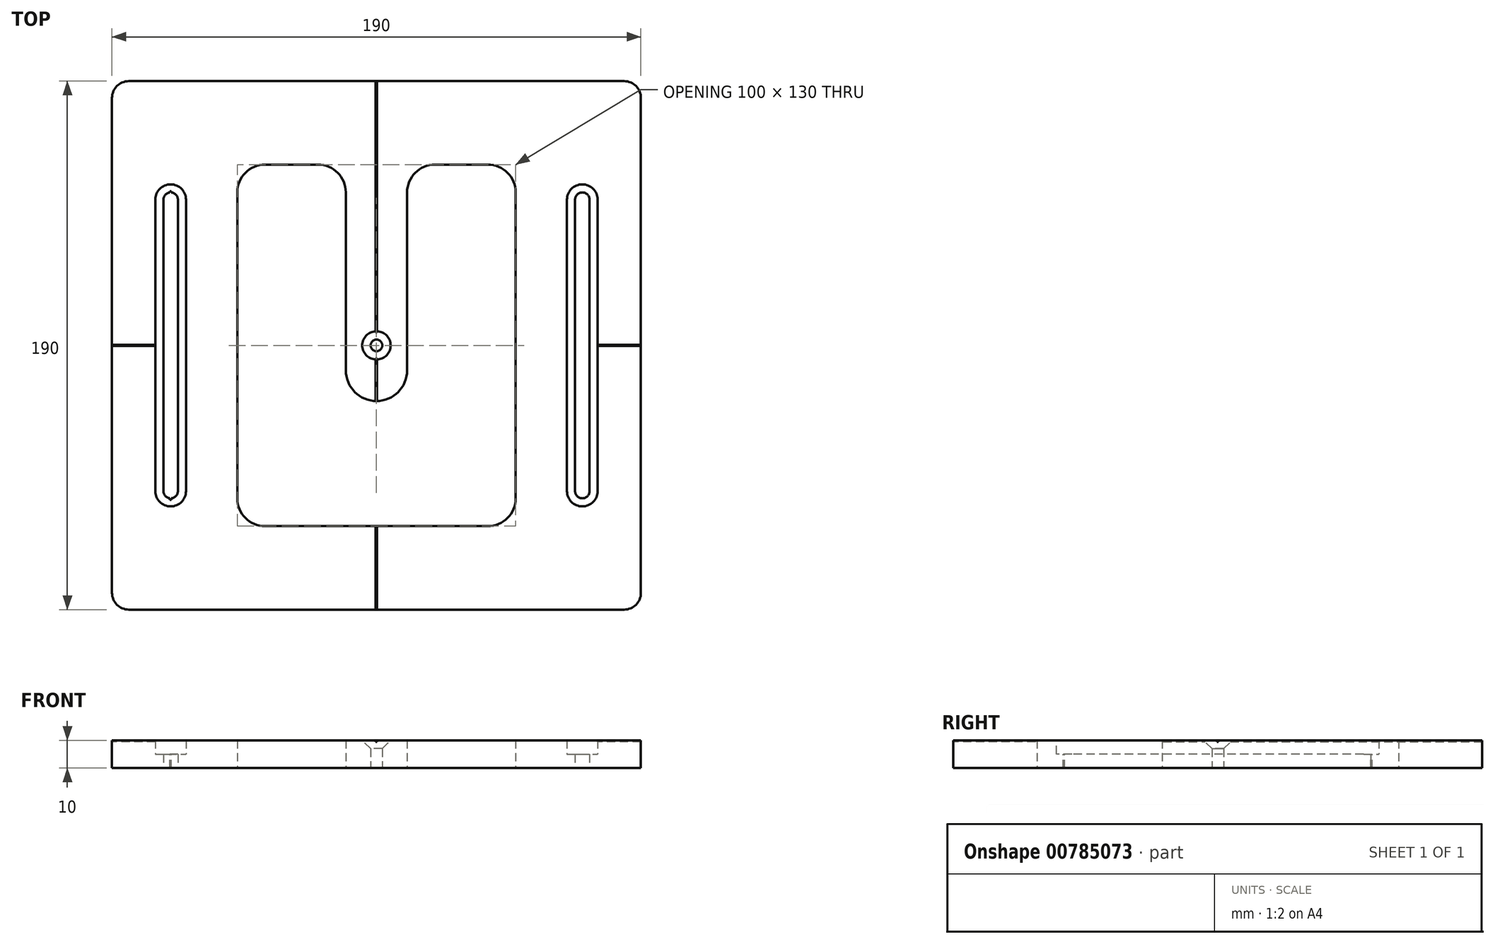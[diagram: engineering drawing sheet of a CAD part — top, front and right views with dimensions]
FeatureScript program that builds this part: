
annotation { "Feature Type Name" : "Feature", "Feature Type Description" : "" }
export const myFeature = defineFeature(function(context is Context, id is Id, definition is map)
    precondition{}
    {
        {
            var Q0;
            Q0=qCreatedBy(makeId("Top.planeOp"),FACE);
            var sketch = newSketch(context, id + "F0", { "sketchPlane" : qUnion([Q0])});
            skLineSegment(sketch, "E0.bottom", {"start": v(95, 95) * mm, "end": v(-95, 95) * mm});
            skLineSegment(sketch, "E0.top", {"start": v(95, -95) * mm, "end": v(-95, -95) * mm});
            skLineSegment(sketch, "E0.left", {"start": v(95, 95) * mm, "end": v(95, -95) * mm});
            skLineSegment(sketch, "E0.right", {"start": v(-95, 95) * mm, "end": v(-95, -95) * mm});
            skPoint(sketch, "E0.middle", {"position": v(0, 0) * mm});
            skLineSegment(sketch, "E1.bottom", {"start": v(40, -65) * mm, "end": v(-40, -65) * mm});
            skLineSegment(sketch, "E1.top", {"start": v(40, 65) * mm, "end": v(21, 65) * mm});
            skLineSegment(sketch, "E1.left", {"start": v(50, -55) * mm, "end": v(50, 55) * mm});
            skLineSegment(sketch, "E1.right", {"start": v(-50, -55) * mm, "end": v(-50, 55) * mm});
            skLineSegment(sketch, "E2", {"start": v(-95, 0) * mm, "end": v(-50, 0) * mm, "construction": true});
            skLineSegment(sketch, "E3.bottom", {"start": v(-76.54, 55) * mm, "end": v(-71.34, 55) * mm});
            skLineSegment(sketch, "E3.top", {"start": v(-76.54, -55) * mm, "end": v(-71.34, -55) * mm});
            skLineSegment(sketch, "E3.left", {"start": v(-76.54, 55) * mm, "end": v(-76.54, -55) * mm});
            skLineSegment(sketch, "E3.right", {"start": v(-71.34, 55) * mm, "end": v(-71.34, -55) * mm});
            skLineSegment(sketch, "E4.MirrorCS", {"start": v(-71.34, -55) * mm, "end": v(-71.34, 55) * mm});
            skLineSegment(sketch, "E5.MirrorCS", {"start": v(-76.54, -55) * mm, "end": v(-76.54, 55) * mm});
            skLineSegment(sketch, "E6.bottom", {"start": v(0, -20) * mm, "end": v(0, -20) * mm});
            skLineSegment(sketch, "E6.left", {"start": v(11, -9) * mm, "end": v(11, 55) * mm});
            skLineSegment(sketch, "E6.right", {"start": v(-11, -9) * mm, "end": v(-11, 55) * mm});
            skPoint(sketch, "E6.middle", {"position": v(0, 22.5) * mm});
            skPoint(sketch, "E7.visualSharp", {"position": v(-11, -20) * mm});
            skArc(sketch, "E7.filletArc", {"start": v(-11, -9) * mm, "mid": v(-7.78, -16.78) * mm, "end": v(0, -20) * mm});
            skPoint(sketch, "E8.visualSharp", {"position": v(11, -20) * mm});
            skArc(sketch, "E8.filletArc", {"start": v(0, -20) * mm, "mid": v(7.78, -16.78) * mm, "end": v(11, -9) * mm});
            skPoint(sketch, "E9.visualSharp", {"position": v(-50, 65) * mm});
            skArc(sketch, "E9.filletArc", {"start": v(-40, 65) * mm, "mid": v(-47.07, 62.07) * mm, "end": v(-50, 55) * mm});
            skPoint(sketch, "E10.visualSharp", {"position": v(50, 65) * mm});
            skArc(sketch, "E10.filletArc", {"start": v(50, 55) * mm, "mid": v(47.07, 62.07) * mm, "end": v(40, 65) * mm});
            skPoint(sketch, "E11.visualSharp", {"position": v(50, -65) * mm});
            skArc(sketch, "E11.filletArc", {"start": v(40, -65) * mm, "mid": v(47.07, -62.07) * mm, "end": v(50, -55) * mm});
            skPoint(sketch, "E12.visualSharp", {"position": v(-50, -65) * mm});
            skArc(sketch, "E12.filletArc", {"start": v(-50, -55) * mm, "mid": v(-47.07, -62.07) * mm, "end": v(-40, -65) * mm});
            skLineSegment(sketch, "E13", {"start": v(-21, 65) * mm, "end": v(-40, 65) * mm});
            skCircle(sketch, "E14", {"center": v(0, 0) * mm, "radius": 2.1 * mm});
            skLineSegment(sketch, "E15.0", {"start": v(-79.44, 57.9) * mm, "end": v(-68.44, 57.9) * mm});
            skLineSegment(sketch, "E15.1", {"start": v(-79.44, 57.9) * mm, "end": v(-79.44, -57.9) * mm});
            skLineSegment(sketch, "E15.2", {"start": v(-79.44, -57.9) * mm, "end": v(-68.44, -57.9) * mm});
            skLineSegment(sketch, "E15.3", {"start": v(-68.44, -57.9) * mm, "end": v(-68.44, 57.9) * mm});
            skPoint(sketch, "E16.visualSharp", {"position": v(11, 65) * mm});
            skArc(sketch, "E16.filletArc", {"start": v(21, 65) * mm, "mid": v(13.93, 62.07) * mm, "end": v(11, 55) * mm});
            skPoint(sketch, "E17.visualSharp", {"position": v(-11, 65) * mm});
            skArc(sketch, "E17.filletArc", {"start": v(-11, 55) * mm, "mid": v(-13.93, 62.07) * mm, "end": v(-21, 65) * mm});
            skLineSegment(sketch, "E18.MirrorCS", {"start": v(68.44, -57.9) * mm, "end": v(68.44, 57.9) * mm});
            skLineSegment(sketch, "E19.MirrorCS", {"start": v(79.44, 57.9) * mm, "end": v(68.44, 57.9) * mm});
            skLineSegment(sketch, "E20.MirrorCS", {"start": v(79.44, 57.9) * mm, "end": v(79.44, -57.9) * mm});
            skLineSegment(sketch, "E21.MirrorCS", {"start": v(79.44, -57.9) * mm, "end": v(68.44, -57.9) * mm});
            skLineSegment(sketch, "E22.MirrorCS", {"start": v(71.34, -55) * mm, "end": v(71.34, 55) * mm});
            skLineSegment(sketch, "E23.MirrorCS", {"start": v(76.54, -55) * mm, "end": v(71.34, -55) * mm});
            skLineSegment(sketch, "E24.MirrorCS", {"start": v(76.54, 55) * mm, "end": v(76.54, -55) * mm});
            skLineSegment(sketch, "E25.MirrorCS", {"start": v(76.54, 55) * mm, "end": v(71.34, 55) * mm});
            skLineSegment(sketch, "E26.bottom", {"start": v(0.25, -65.5) * mm, "end": v(-0.25, -65.5) * mm});
            skLineSegment(sketch, "E26.top", {"start": v(0.25, -64.5) * mm, "end": v(-0.25, -64.5) * mm});
            skLineSegment(sketch, "E26.left", {"start": v(0.25, -65.5) * mm, "end": v(0.25, -64.5) * mm});
            skLineSegment(sketch, "E26.right", {"start": v(-0.25, -65.5) * mm, "end": v(-0.25, -64.5) * mm});
            skPoint(sketch, "E26.middle", {"position": v(0, -65) * mm});
            skLineSegment(sketch, "E27.bottom", {"start": v(0.25, -19.5) * mm, "end": v(-0.25, -19.5) * mm});
            skLineSegment(sketch, "E27.top", {"start": v(0.25, -20.5) * mm, "end": v(-0.25, -20.5) * mm});
            skLineSegment(sketch, "E27.left", {"start": v(0.25, -19.5) * mm, "end": v(0.25, -20.5) * mm});
            skLineSegment(sketch, "E27.right", {"start": v(-0.25, -19.5) * mm, "end": v(-0.25, -20.5) * mm});
            skPoint(sketch, "E27.middle", {"position": v(0, -20) * mm});
            skSolve(sketch);
        }
        {
            var Q0;
            Q0=makeQuery(id+"F0.imprint","IMPRINT",FACE,{"disambiguationData":[TD([[makeQuery(id+"F0.imprint","IMPRINT",EDGE,{"derivedFrom":sQuery(id+"F0.wireOp",EDGE,"E0.bottom")}),1.0]])]});
            var Q1;
            {var subQ1=sQuery(id+"F0.wireOp",EDGE,"E27.bottom");Q1=makeQuery(id+"F0.imprint","IMPRINT",FACE,{"disambiguationData":[TD([[makeQuery(id+"F0.imprint","IMPRINT",EDGE,{"derivedFrom":subQ1}),1.0]])]});}
            var Q2;
            {var subQ5=sQuery(id+"F0.wireOp",EDGE,"E26.bottom");Q2=makeQuery(id+"F0.imprint","IMPRINT",FACE,{"disambiguationData":[TD([[makeQuery(id+"F0.imprint","IMPRINT",EDGE,{"derivedFrom":subQ5}),-1.0]])]});}
            extrude(context, id + "F1", {"entities" : qUnion([Q0, Q1, Q2]), "depth" : 10 * mm, "offsetDistance" : 25 * mm});
        }
        {
            var Q0;
            Q0=makeQuery(id+"F0.imprint","IMPRINT",FACE,{"disambiguationData":[TD([[makeQuery(id+"F0.imprint","IMPRINT",EDGE,{"derivedFrom":sQuery(id+"F0.wireOp",EDGE,"E3.bottom")}),1.0]])]});
            var Q1;
            Q1=makeQuery(id+"F0.imprint","IMPRINT",FACE,{"disambiguationData":[TD([[makeQuery(id+"F0.imprint","IMPRINT",EDGE,{"derivedFrom":sQuery(id+"F0.wireOp",EDGE,"E18.MirrorCS")}),-1.0]])]});
            extrude(context, id + "F2", {"entities" : qUnion([Q0, Q1]), "operationType" : NewBodyOperationType.ADD, "depth" : 5 * mm, "offsetDistance" : 25 * mm});
        }
        {
            var Q0;
            Q0=makeQuery(id+"F2.opExtrude","SWEPT_EDGE",EDGE,{"disambiguationData":[OSD([sQuery(id+"F0.wireOp",EDGE,"E3.bottom"),sQuery(id+"F0.wireOp",EDGE,"E3.left")])]});
            var Q1;
            Q1=makeQuery(id+"F2.opExtrude","SWEPT_EDGE",EDGE,{"disambiguationData":[OSD([sQuery(id+"F0.wireOp",EDGE,"E3.bottom"),sQuery(id+"F0.wireOp",EDGE,"E3.right")])]});
            var Q2;
            Q2=makeQuery(id+"F2.opExtrude","SWEPT_EDGE",EDGE,{"disambiguationData":[OSD([sQuery(id+"F0.wireOp",EDGE,"E3.top"),sQuery(id+"F0.wireOp",EDGE,"E3.left")])]});
            var Q3;
            Q3=makeQuery(id+"F2.opExtrude","SWEPT_EDGE",EDGE,{"disambiguationData":[OSD([sQuery(id+"F0.wireOp",EDGE,"E3.top"),sQuery(id+"F0.wireOp",EDGE,"E3.right")])]});
            var Q4;
            Q4=makeQuery(id+"F2.opExtrude","SWEPT_EDGE",EDGE,{"disambiguationData":[OSD([sQuery(id+"F0.wireOp",EDGE,"E23.MirrorCS"),sQuery(id+"F0.wireOp",EDGE,"E24.MirrorCS")])]});
            var Q5;
            Q5=makeQuery(id+"F2.opExtrude","SWEPT_EDGE",EDGE,{"disambiguationData":[OSD([sQuery(id+"F0.wireOp",EDGE,"E22.MirrorCS"),sQuery(id+"F0.wireOp",EDGE,"E23.MirrorCS")])]});
            var Q6;
            Q6=makeQuery(id+"F2.opExtrude","SWEPT_EDGE",EDGE,{"disambiguationData":[OSD([sQuery(id+"F0.wireOp",EDGE,"E22.MirrorCS"),sQuery(id+"F0.wireOp",EDGE,"E25.MirrorCS")])]});
            var Q7;
            Q7=makeQuery(id+"F2.opExtrude","SWEPT_EDGE",EDGE,{"disambiguationData":[OSD([sQuery(id+"F0.wireOp",EDGE,"E24.MirrorCS"),sQuery(id+"F0.wireOp",EDGE,"E25.MirrorCS")])]});
            fillet(context, id + "F3", {"entities" : qUnion([Q0, Q1, Q2, Q3, Q4, Q5, Q6, Q7]), "radius" : 2.6 * mm, "tangentPropagation" : true, "allowEdgeOverflow" : false});
        }
        {
            var Q0;
            Q0=makeQuery(id+"F1.opExtrude","SWEPT_EDGE",EDGE,{"disambiguationData":[OSD([sQuery(id+"F0.wireOp",EDGE,"E15.0"),sQuery(id+"F0.wireOp",EDGE,"E15.1")])]});
            var Q1;
            Q1=makeQuery(id+"F1.opExtrude","SWEPT_EDGE",EDGE,{"disambiguationData":[OSD([sQuery(id+"F0.wireOp",EDGE,"E15.0"),sQuery(id+"F0.wireOp",EDGE,"E15.3")])]});
            var Q2;
            Q2=makeQuery(id+"F1.opExtrude","SWEPT_EDGE",EDGE,{"disambiguationData":[OSD([sQuery(id+"F0.wireOp",EDGE,"E19.MirrorCS"),sQuery(id+"F0.wireOp",EDGE,"E20.MirrorCS")])]});
            var Q3;
            Q3=makeQuery(id+"F1.opExtrude","SWEPT_EDGE",EDGE,{"disambiguationData":[OSD([sQuery(id+"F0.wireOp",EDGE,"E18.MirrorCS"),sQuery(id+"F0.wireOp",EDGE,"E19.MirrorCS")])]});
            var Q4;
            Q4=makeQuery(id+"F1.opExtrude","SWEPT_EDGE",EDGE,{"disambiguationData":[OSD([sQuery(id+"F0.wireOp",EDGE,"E18.MirrorCS"),sQuery(id+"F0.wireOp",EDGE,"E21.MirrorCS")])]});
            var Q5;
            Q5=makeQuery(id+"F1.opExtrude","SWEPT_EDGE",EDGE,{"disambiguationData":[OSD([sQuery(id+"F0.wireOp",EDGE,"E20.MirrorCS"),sQuery(id+"F0.wireOp",EDGE,"E21.MirrorCS")])]});
            var Q6;
            Q6=makeQuery(id+"F1.opExtrude","SWEPT_EDGE",EDGE,{"disambiguationData":[OSD([sQuery(id+"F0.wireOp",EDGE,"E15.1"),sQuery(id+"F0.wireOp",EDGE,"E15.2")])]});
            var Q7;
            Q7=makeQuery(id+"F1.opExtrude","SWEPT_EDGE",EDGE,{"disambiguationData":[OSD([sQuery(id+"F0.wireOp",EDGE,"E15.2"),sQuery(id+"F0.wireOp",EDGE,"E15.3")])]});
            fillet(context, id + "F4", {"entities" : qUnion([Q0, Q1, Q2, Q3, Q4, Q5, Q6, Q7]), "radius" : 5.5 * mm, "tangentPropagation" : true, "allowEdgeOverflow" : false});
        }
        {
            var Q0;
            Q0=makeQuery(id+"F2.opExtrude","CAP_FACE",FACE,{"disambiguationData":[OSD([sQuery(id+"F0.wireOp",EDGE,"E3.bottom"),sQuery(id+"F0.wireOp",EDGE,"E3.top"),sQuery(id+"F0.wireOp",EDGE,"E3.right"),sQuery(id+"F0.wireOp",EDGE,"E3.left"),sQuery(id+"F0.wireOp",EDGE,"E15.0"),sQuery(id+"F0.wireOp",EDGE,"E15.1"),sQuery(id+"F0.wireOp",EDGE,"E15.2"),sQuery(id+"F0.wireOp",EDGE,"E15.3")])],"isStart":false});
            var sketch = newSketch(context, id + "F5", { "sketchPlane" : qUnion([Q0])});
            skLineSegment(sketch, "E28.bottom", {"start": v(-73.69, 54.5) * mm, "end": v(-74.19, 54.5) * mm});
            skLineSegment(sketch, "E28.top", {"start": v(-73.69, 55.5) * mm, "end": v(-74.19, 55.5) * mm});
            skLineSegment(sketch, "E28.left", {"start": v(-73.69, 54.5) * mm, "end": v(-73.69, 55.5) * mm});
            skLineSegment(sketch, "E28.right", {"start": v(-74.19, 54.5) * mm, "end": v(-74.19, 55.5) * mm});
            skPoint(sketch, "E28.middle", {"position": v(-73.94, 55) * mm});
            skLineSegment(sketch, "E29.bottom", {"start": v(-73.69, -55.5) * mm, "end": v(-74.19, -55.5) * mm});
            skLineSegment(sketch, "E29.top", {"start": v(-73.69, -54.5) * mm, "end": v(-74.19, -54.5) * mm});
            skLineSegment(sketch, "E29.left", {"start": v(-73.69, -55.5) * mm, "end": v(-73.69, -54.5) * mm});
            skLineSegment(sketch, "E29.right", {"start": v(-74.19, -55.5) * mm, "end": v(-74.19, -54.5) * mm});
            skPoint(sketch, "E29.middle", {"position": v(-73.94, -55) * mm});
            skSolve(sketch);
        }
        {
            var Q0;
            {var subQ0=sQuery(id+"F5.wireOp",EDGE,"E29.bottom");Q0=makeQuery(id+"F5.imprint","IMPRINT",FACE,{"disambiguationData":[TD([[makeQuery(id+"F5.imprint","IMPRINT",EDGE,{"derivedFrom":subQ0}),-1.0]])]});}
            var Q1;
            {var subQ0=sQuery(id+"F5.wireOp",EDGE,"E28.top");Q1=makeQuery(id+"F5.imprint","IMPRINT",FACE,{"disambiguationData":[TD([[makeQuery(id+"F5.imprint","IMPRINT",EDGE,{"derivedFrom":subQ0}),1.0]])]});}
            extrude(context, id + "F6", {"entities" : qUnion([Q0, Q1]), "operationType" : NewBodyOperationType.REMOVE, "oppositeDirection" : true, "depth" : 25 * mm, "offsetDistance" : 25 * mm});
        }
        {
            var Q0;
            Q0=makeQuery(id+"F1.opExtrude","CAP_FACE",FACE,{"disambiguationData":[OSD([sQuery(id+"F0.wireOp",EDGE,"E0.bottom"),sQuery(id+"F0.wireOp",EDGE,"E0.top"),sQuery(id+"F0.wireOp",EDGE,"E0.left"),sQuery(id+"F0.wireOp",EDGE,"E0.right"),sQuery(id+"F0.wireOp",EDGE,"E1.bottom"),sQuery(id+"F0.wireOp",EDGE,"E1.top"),sQuery(id+"F0.wireOp",EDGE,"E1.left"),sQuery(id+"F0.wireOp",EDGE,"E1.right"),sQuery(id+"F0.wireOp",EDGE,"E6.left"),sQuery(id+"F0.wireOp",EDGE,"E6.right"),sQuery(id+"F0.wireOp",EDGE,"E7.filletArc"),sQuery(id+"F0.wireOp",EDGE,"E8.filletArc"),sQuery(id+"F0.wireOp",EDGE,"E9.filletArc"),sQuery(id+"F0.wireOp",EDGE,"E10.filletArc"),sQuery(id+"F0.wireOp",EDGE,"E11.filletArc"),sQuery(id+"F0.wireOp",EDGE,"E12.filletArc"),sQuery(id+"F0.wireOp",EDGE,"E13"),sQuery(id+"F0.wireOp",EDGE,"0993da1e-e7eb-4dab-95c8-7e407798bd87.0"),sQuery(id+"F0.wireOp",EDGE,"E15.0"),sQuery(id+"F0.wireOp",EDGE,"E15.1"),sQuery(id+"F0.wireOp",EDGE,"E15.2"),sQuery(id+"F0.wireOp",EDGE,"E15.3"),sQuery(id+"F0.wireOp",EDGE,"E16.filletArc"),sQuery(id+"F0.wireOp",EDGE,"E17.filletArc"),sQuery(id+"F0.wireOp",EDGE,"E18.MirrorCS"),sQuery(id+"F0.wireOp",EDGE,"E19.MirrorCS"),sQuery(id+"F0.wireOp",EDGE,"E20.MirrorCS"),sQuery(id+"F0.wireOp",EDGE,"E21.MirrorCS")])],"isStart":false});
            var sketch = newSketch(context, id + "F7", { "sketchPlane" : qUnion([Q0])});
            skLineSegment(sketch, "E30.bottom", {"start": v(-0.25, -19.6) * mm, "end": v(0.25, -19.6) * mm});
            skLineSegment(sketch, "E30.top", {"start": v(-0.25, -20.4) * mm, "end": v(0.25, -20.4) * mm});
            skLineSegment(sketch, "E30.left", {"start": v(-0.25, -19.6) * mm, "end": v(-0.25, -20.4) * mm});
            skLineSegment(sketch, "E30.right", {"start": v(0.25, -19.6) * mm, "end": v(0.25, -20.4) * mm});
            skPoint(sketch, "E30.middle", {"position": v(0, -20) * mm});
            skLineSegment(sketch, "E31.bottom", {"start": v(0.25, -64.5) * mm, "end": v(-0.25, -64.5) * mm});
            skLineSegment(sketch, "E31.top", {"start": v(0.25, -65.5) * mm, "end": v(-0.25, -65.5) * mm});
            skLineSegment(sketch, "E31.left", {"start": v(0.25, -64.5) * mm, "end": v(0.25, -65.5) * mm});
            skLineSegment(sketch, "E31.right", {"start": v(-0.25, -64.5) * mm, "end": v(-0.25, -65.5) * mm});
            skPoint(sketch, "E31.middle", {"position": v(0, -65) * mm});
            skLineSegment(sketch, "E32.bottom", {"start": v(-0.25, -65.5) * mm, "end": v(0.25, -65.5) * mm});
            skLineSegment(sketch, "E32.top", {"start": v(-0.25, -65.5) * mm, "end": v(0.25, -65.5) * mm});
            skLineSegment(sketch, "E32.left", {"start": v(-0.25, -65.5) * mm, "end": v(-0.25, -65.5) * mm});
            skLineSegment(sketch, "E32.right", {"start": v(0.25, -65.5) * mm, "end": v(0.25, -65.5) * mm});
            skLineSegment(sketch, "E33.top", {"start": v(0.25, -95) * mm, "end": v(-0.25, -95) * mm});
            skLineSegment(sketch, "E33.left", {"start": v(0.25, -65.5) * mm, "end": v(0.25, -95) * mm});
            skLineSegment(sketch, "E33.right", {"start": v(-0.25, -65.5) * mm, "end": v(-0.25, -95) * mm});
            skLineSegment(sketch, "E34.top", {"start": v(-0.25, 95) * mm, "end": v(0.25, 95) * mm});
            skLineSegment(sketch, "E34.left", {"start": v(-0.25, -19.6) * mm, "end": v(-0.25, 95) * mm});
            skLineSegment(sketch, "E34.right", {"start": v(0.25, -19.6) * mm, "end": v(0.25, 95) * mm});
            skLineSegment(sketch, "E35.bottom", {"start": v(95, -0.25) * mm, "end": v(-95.5, -0.25) * mm});
            skLineSegment(sketch, "E35.top", {"start": v(95, 0.25) * mm, "end": v(-95.5, 0.25) * mm});
            skLineSegment(sketch, "E35.left", {"start": v(95, -0.25) * mm, "end": v(95, 0.25) * mm});
            skLineSegment(sketch, "E35.right", {"start": v(-95.5, -0.25) * mm, "end": v(-95.5, 0.25) * mm});
            skPoint(sketch, "E35.middle", {"position": v(-0.25, 0) * mm});
            skSolve(sketch);
        }
        {
            var Q0;
            Q0=makeQuery(id+"F1.opExtrude","SWEPT_EDGE",EDGE,{"disambiguationData":[OSD([sQuery(id+"F0.wireOp",EDGE,"E0.top"),sQuery(id+"F0.wireOp",EDGE,"E0.right")])]});
            var Q1;
            Q1=makeQuery(id+"F1.opExtrude","SWEPT_EDGE",EDGE,{"disambiguationData":[OSD([sQuery(id+"F0.wireOp",EDGE,"E0.top"),sQuery(id+"F0.wireOp",EDGE,"E0.left")])]});
            var Q2;
            Q2=makeQuery(id+"F1.opExtrude","SWEPT_EDGE",EDGE,{"disambiguationData":[OSD([sQuery(id+"F0.wireOp",EDGE,"E0.bottom"),sQuery(id+"F0.wireOp",EDGE,"E0.left")])]});
            var Q3;
            Q3=makeQuery(id+"F1.opExtrude","SWEPT_EDGE",EDGE,{"disambiguationData":[OSD([sQuery(id+"F0.wireOp",EDGE,"E0.bottom"),sQuery(id+"F0.wireOp",EDGE,"E0.right")])]});
            fillet(context, id + "F8", {"entities" : qUnion([Q0, Q1, Q2, Q3]), "radius" : 6 * mm, "tangentPropagation" : true, "allowEdgeOverflow" : false});
        }
        {
            var Q0;
            {var subQ0=sQuery(id+"F7.wireOp",EDGE,"E34.top");Q0=makeQuery(id+"F7.imprint","IMPRINT",FACE,{"disambiguationData":[TD([[makeQuery(id+"F7.imprint","IMPRINT",EDGE,{"derivedFrom":subQ0}),1.0]])]});}
            var Q1;
            {var subQ0=sQuery(id+"F7.wireOp",EDGE,"E30.bottom");Q1=makeQuery(id+"F7.imprint","IMPRINT",FACE,{"disambiguationData":[TD([[makeQuery(id+"F7.imprint","IMPRINT",EDGE,{"derivedFrom":subQ0}),1.0]])]});}
            var Q2;
            Q2=makeQuery(id+"F7.imprint","IMPRINT",FACE,{"disambiguationData":[TD([[makeQuery(id+"F7.imprint","IMPRINT",EDGE,{"derivedFrom":sQuery(id+"F7.wireOp",EDGE,"E31.top")}),1.0]])]});
            var Q3;
            {var subQ0=sQuery(id+"F7.wireOp",EDGE,"E35.bottom");var subQ1=sQuery(id+"F7.wireOp",EDGE,"E34.left");var subQ2=makeQuery(id+"F7.imprint","INTERSECT",VERTEX,{"derivedFrom":[subQ1,subQ0]});Q3=makeQuery(id+"F7.imprint","IMPRINT",FACE,{"disambiguationData":[TD([[makeQuery(id+"F7.imprint","IMPRINT",EDGE,{"disambiguationData":[TD([[subQ2,1.0]])],"derivedFrom":subQ0}),1.0]])]});}
            var Q4;
            {var subQ0=sQuery(id+"F7.wireOp",EDGE,"E35.top");var subQ1=sQuery(id+"F7.wireOp",EDGE,"E34.left");var subQ2=makeQuery(id+"F7.imprint","INTERSECT",VERTEX,{"derivedFrom":[subQ1,subQ0]});Q4=makeQuery(id+"F7.imprint","IMPRINT",FACE,{"disambiguationData":[TD([[makeQuery(id+"F7.imprint","IMPRINT",EDGE,{"disambiguationData":[TD([[subQ2,1.0]])],"derivedFrom":subQ0}),-1.0]])]});}
            extrude(context, id + "F9", {"entities" : qUnion([Q0, Q1, Q2, Q3, Q4]), "operationType" : NewBodyOperationType.REMOVE, "oppositeDirection" : true, "depth" : 0.5 * mm, "offsetDistance" : 25 * mm});
        }
        {
            var Q0;
            {var subQ0=sQuery(id+"F7.wireOp",EDGE,"E35.left");Q0=makeQuery(id+"F7.imprint","IMPRINT",FACE,{"disambiguationData":[TD([[makeQuery(id+"F7.imprint","IMPRINT",EDGE,{"derivedFrom":subQ0}),-1.0]])]});}
            var Q1;
            {var subQ0=sQuery(id+"F7.wireOp",EDGE,"E35.bottom");var subQ1=makeQuery(id+"F1.opExtrude","CAP_EDGE",EDGE,{"disambiguationData":[OSD([sQuery(id+"F0.wireOp",EDGE,"E0.right")])],"isStart":false});var subQ2=makeQuery(id+"F7.imprint","INTERSECT",VERTEX,{"derivedFrom":[subQ1,subQ0]});Q1=makeQuery(id+"F7.imprint","IMPRINT",FACE,{"disambiguationData":[TD([[makeQuery(id+"F7.imprint","IMPRINT",EDGE,{"disambiguationData":[TD([[subQ2,1.0]])],"derivedFrom":subQ0}),-1.0]])]});}
            extrude(context, id + "F10", {"entities" : qUnion([Q0, Q1]), "operationType" : NewBodyOperationType.REMOVE, "oppositeDirection" : true, "depth" : 0.5 * mm, "offsetDistance" : 25 * mm});
        }
        {
            var Q0;
            {var subQ0=sQuery(id+"F0.wireOp",EDGE,"E14");var subQ2=sQuery(id+"F7.wireOp",EDGE,"E34.left");var subQ3=makeQuery(id+"F1.opExtrude","CAP_EDGE",EDGE,{"disambiguationData":[OSD([subQ0])],"isStart":false});var subQ4=makeQuery(id+"F7.imprint","INTERSECT",VERTEX,{"disambiguationData":[OD(0.0)],"derivedFrom":[subQ3,subQ2]});Q0=makeQuery(id+"F9.boolean.opBoolean","SPLIT",EDGE,{"disambiguationData":[TD([makeQuery(id+"F9.opExtrude","SWEPT_FACE",FACE,{"disambiguationData":[OSD([subQ2]),TDD([makeQuery(id+"F7.imprint","IMPRINT",EDGE,{"disambiguationData":[TD([[subQ4,1.0]])],"derivedFrom":subQ2}),makeQuery(id+"F7.imprint","IMPRINT",EDGE,{"disambiguationData":[TD([[makeQuery(id+"F7.imprint","INTERSECT",VERTEX,{"derivedFrom":[subQ2,sQuery(id+"F7.wireOp",EDGE,"E35.bottom")]}),1.0]])],"derivedFrom":subQ2})])]})])],"derivedFrom":subQ3});}
            chamfer(context, id + "F11", {"entities" : qUnion([Q0]), "width" : 3 * mm, "tangentPropagation" : true});
        }
    });
